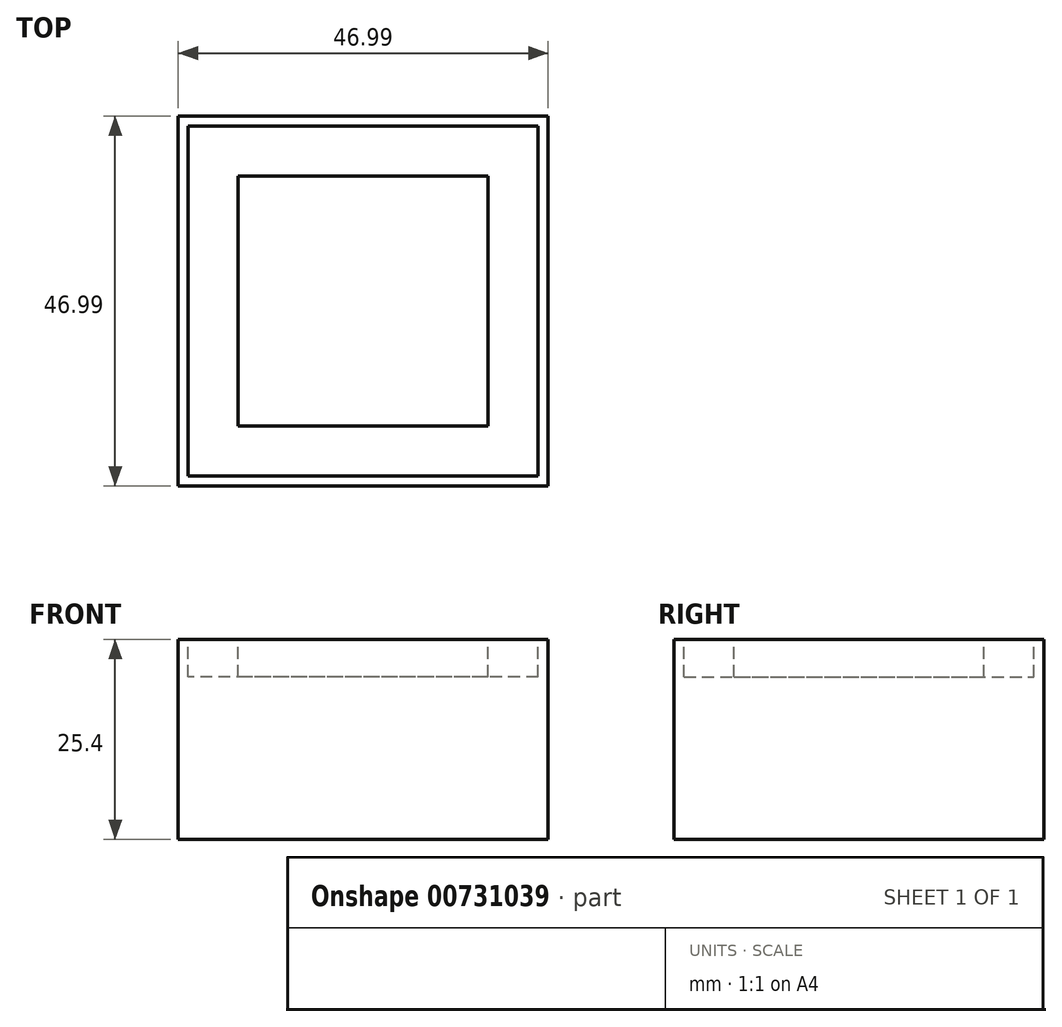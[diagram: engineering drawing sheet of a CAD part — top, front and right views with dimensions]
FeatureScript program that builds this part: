
annotation { "Feature Type Name" : "Feature", "Feature Type Description" : "" }
export const myFeature = defineFeature(function(context is Context, id is Id, definition is map)
    precondition{}
    {
        {
            var Q0;
            Q0=qCreatedBy(makeId("Top.planeOp"),FACE);
            var sketch = newSketch(context, id + "F0", { "sketchPlane" : qUnion([Q0])});
            skLineSegment(sketch, "E0.bottom", {"start": v(0, 0) * mm, "end": v(-47, 0) * mm});
            skLineSegment(sketch, "E0.top", {"start": v(0, 47) * mm, "end": v(-47, 46.99) * mm});
            skLineSegment(sketch, "E0.left", {"start": v(0, 0) * mm, "end": v(0, 47) * mm});
            skLineSegment(sketch, "E0.right", {"start": v(-47, 0) * mm, "end": v(-47, 46.99) * mm});
            skLineSegment(sketch, "E1.0", {"start": v(-45.72, 1.27) * mm, "end": v(-45.72, 45.72) * mm});
            skLineSegment(sketch, "E1.1", {"start": v(-1.27, 1.27) * mm, "end": v(-45.72, 1.27) * mm});
            skLineSegment(sketch, "E1.2", {"start": v(-1.27, 1.27) * mm, "end": v(-1.27, 45.72) * mm});
            skLineSegment(sketch, "E1.3", {"start": v(-1.27, 45.72) * mm, "end": v(-45.72, 45.72) * mm});
            skLineSegment(sketch, "E2.0", {"start": v(-39.37, 7.62) * mm, "end": v(-39.37, 39.37) * mm});
            skLineSegment(sketch, "E2.1", {"start": v(-7.62, 7.62) * mm, "end": v(-39.37, 7.62) * mm});
            skLineSegment(sketch, "E2.2", {"start": v(-7.62, 7.62) * mm, "end": v(-7.62, 39.37) * mm});
            skLineSegment(sketch, "E2.3", {"start": v(-7.62, 39.37) * mm, "end": v(-39.37, 39.37) * mm});
            skSolve(sketch);
        }
        {
            var Q0;
            Q0=makeQuery(id+"F0.imprint","IMPRINT",FACE,{"disambiguationData":[TD([[makeQuery(id+"F0.imprint","IMPRINT",EDGE,{"derivedFrom":sQuery(id+"F0.wireOp",EDGE,"E0.bottom")}),-1.0]])]});
            var Q1;
            Q1=makeQuery(id+"F0.imprint","IMPRINT",FACE,{"disambiguationData":[TD([[makeQuery(id+"F0.imprint","IMPRINT",EDGE,{"derivedFrom":sQuery(id+"F0.wireOp",EDGE,"E1.0")}),-1.0]])]});
            var Q2;
            Q2=makeQuery(id+"F0.imprint","IMPRINT",FACE,{"disambiguationData":[TD([[makeQuery(id+"F0.imprint","IMPRINT",EDGE,{"derivedFrom":sQuery(id+"F0.wireOp",EDGE,"E2.0")}),-1.0]])]});
            extrude(context, id + "F1", {"entities" : qUnion([Q0, Q1, Q2]), "oppositeDirection" : true, "depth" : 25.4 * mm, "offsetDistance" : 25.4 * mm});
        }
        {
            var Q0;
            Q0=makeQuery(id+"F0.imprint","IMPRINT",FACE,{"disambiguationData":[TD([[makeQuery(id+"F0.imprint","IMPRINT",EDGE,{"derivedFrom":sQuery(id+"F0.wireOp",EDGE,"E1.0")}),-1.0]])]});
            extrude(context, id + "F2", {"entities" : qUnion([Q0]), "operationType" : NewBodyOperationType.REMOVE, "oppositeDirection" : true, "depth" : 4.76 * mm, "offsetDistance" : 25.4 * mm});
        }
    });
